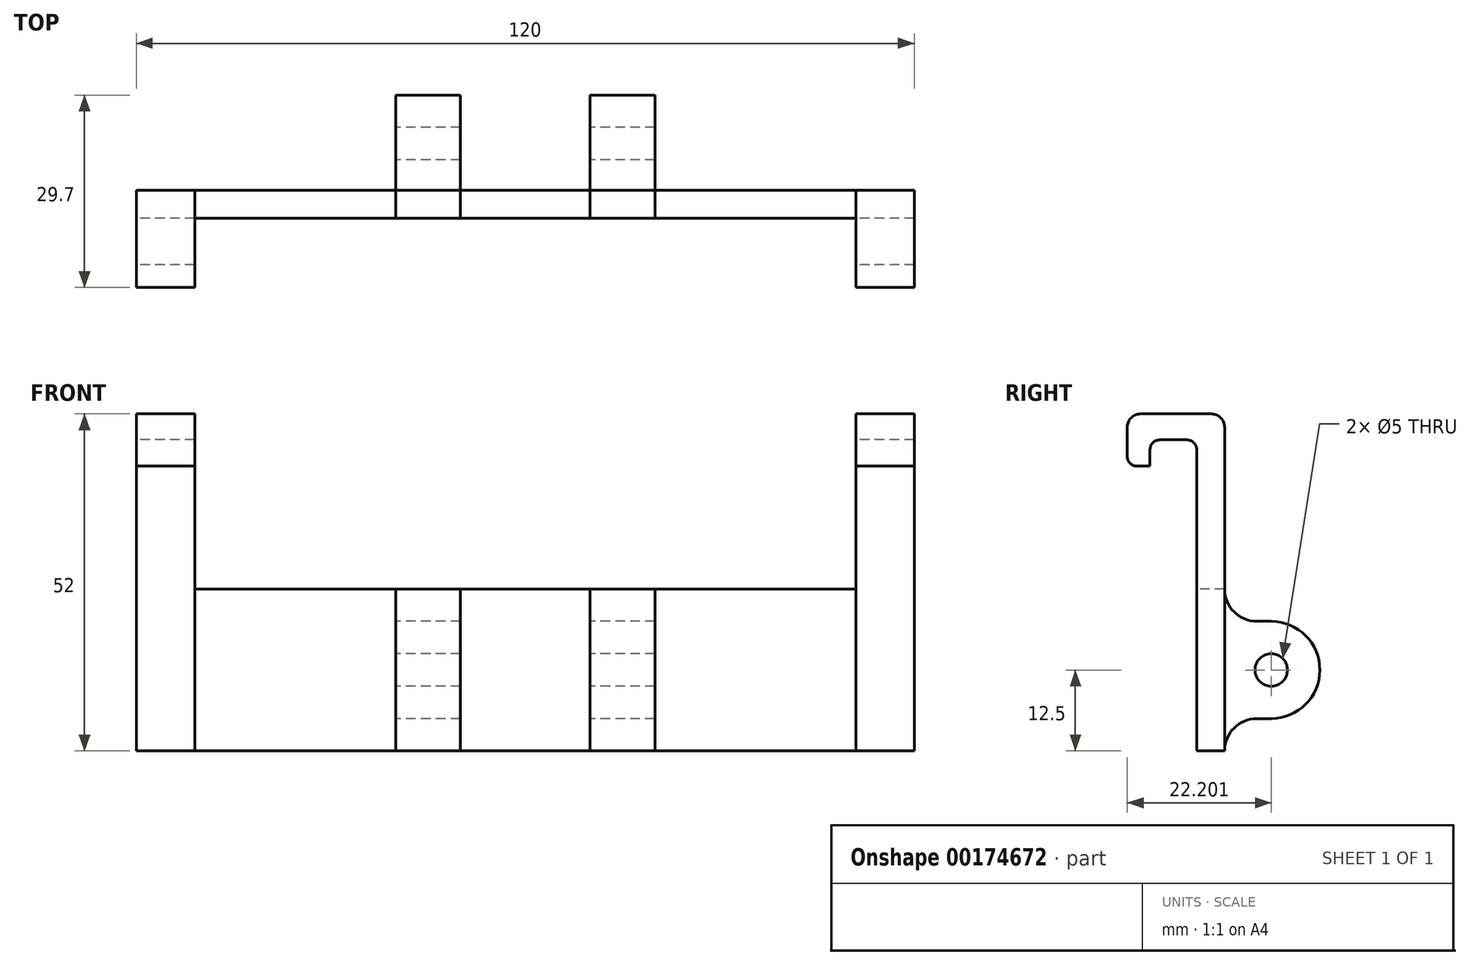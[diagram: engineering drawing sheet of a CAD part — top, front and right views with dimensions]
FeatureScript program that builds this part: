
annotation { "Feature Type Name" : "Feature", "Feature Type Description" : "" }
export const myFeature = defineFeature(function(context is Context, id is Id, definition is map)
    precondition{}
    {
        {
            var Q0;
            Q0=qCreatedBy(makeId("Right.planeOp"),FACE);
            var sketch = newSketch(context, id + "F0", { "sketchPlane" : qUnion([Q0])});
            skLineSegment(sketch, "E0", {"start": v(-3, 12.5) * mm, "end": v(-3, 37.5) * mm});
            skLineSegment(sketch, "E1", {"start": v(-5, 39.5) * mm, "end": v(-16, 39.5) * mm});
            skLineSegment(sketch, "E2", {"start": v(-18, 37.5) * mm, "end": v(-18, 32.94) * mm});
            skLineSegment(sketch, "E3", {"start": v(-16.5, 31.44) * mm, "end": v(-14.5, 31.44) * mm});
            skLineSegment(sketch, "E4", {"start": v(-14.5, 31.44) * mm, "end": v(-14.5, 34) * mm});
            skLineSegment(sketch, "E5", {"start": v(-13, 35.5) * mm, "end": v(-8.8, 35.5) * mm});
            skLineSegment(sketch, "E6", {"start": v(-7.3, 34) * mm, "end": v(-7.3, 0) * mm});
            skArc(sketch, "E7", {"start": v(4.2, -7.5) * mm, "mid": v(11.7, 0) * mm, "end": v(4.2, 7.5) * mm});
            skCircle(sketch, "E8", {"center": v(4.2, 0) * mm, "radius": 2.5 * mm});
            skLineSegment(sketch, "E9", {"start": v(4.2, 7.5) * mm, "end": v(2, 7.5) * mm});
            skPoint(sketch, "E10.newPointA", {"position": v(-3, 2.1) * mm});
            skArc(sketch, "E10.filletArc", {"start": v(-3, 12.5) * mm, "mid": v(-1.54, 8.96) * mm, "end": v(2, 7.5) * mm});
            skPoint(sketch, "E11.visualSharp", {"position": v(-3, 39.5) * mm});
            skArc(sketch, "E11.filletArc", {"start": v(-3, 37.5) * mm, "mid": v(-3.59, 38.91) * mm, "end": v(-5, 39.5) * mm});
            skPoint(sketch, "E12.visualSharp", {"position": v(-18, 39.5) * mm});
            skArc(sketch, "E12.filletArc", {"start": v(-16, 39.5) * mm, "mid": v(-17.41, 38.91) * mm, "end": v(-18, 37.5) * mm});
            skPoint(sketch, "E13.visualSharp", {"position": v(-7.3, 35.5) * mm});
            skArc(sketch, "E13.filletArc", {"start": v(-7.3, 34) * mm, "mid": v(-7.74, 35.06) * mm, "end": v(-8.8, 35.5) * mm});
            skPoint(sketch, "E14.visualSharp", {"position": v(-14.5, 35.5) * mm});
            skArc(sketch, "E14.filletArc", {"start": v(-13, 35.5) * mm, "mid": v(-14.06, 35.06) * mm, "end": v(-14.5, 34) * mm});
            skPoint(sketch, "E15.visualSharp", {"position": v(-18, 31.44) * mm});
            skArc(sketch, "E15.filletArc", {"start": v(-18, 32.94) * mm, "mid": v(-17.56, 31.88) * mm, "end": v(-16.5, 31.44) * mm});
            skLineSegment(sketch, "E16.MirrorCS", {"start": v(-7.3, -34) * mm, "end": v(-7.3, 0) * mm});
            skArc(sketch, "E17.MirrorCS", {"start": v(-7.3, -34) * mm, "mid": v(-7.74, -35.06) * mm, "end": v(-8.8, -35.5) * mm});
            skLineSegment(sketch, "E18.MirrorCS", {"start": v(-13, -35.5) * mm, "end": v(-8.8, -35.5) * mm});
            skArc(sketch, "E19.MirrorCS", {"start": v(-13, -35.5) * mm, "mid": v(-14.06, -35.06) * mm, "end": v(-14.5, -34) * mm});
            skLineSegment(sketch, "E20.MirrorCS", {"start": v(-14.5, -31.44) * mm, "end": v(-14.5, -34) * mm});
            skLineSegment(sketch, "E21.MirrorCS", {"start": v(-16.5, -31.44) * mm, "end": v(-14.5, -31.44) * mm});
            skArc(sketch, "E22.MirrorCS", {"start": v(-18, -32.94) * mm, "mid": v(-17.56, -31.88) * mm, "end": v(-16.5, -31.44) * mm});
            skLineSegment(sketch, "E23.MirrorCS", {"start": v(-18, -37.5) * mm, "end": v(-18, -32.94) * mm});
            skArc(sketch, "E24.MirrorCS", {"start": v(-16, -39.5) * mm, "mid": v(-17.41, -38.91) * mm, "end": v(-18, -37.5) * mm});
            skLineSegment(sketch, "E25.MirrorCS", {"start": v(-5, -39.5) * mm, "end": v(-16, -39.5) * mm});
            skArc(sketch, "E26.MirrorCS", {"start": v(-3, -37.5) * mm, "mid": v(-3.59, -38.91) * mm, "end": v(-5, -39.5) * mm});
            skLineSegment(sketch, "E27.MirrorCS", {"start": v(-3, -12.5) * mm, "end": v(-3, -37.5) * mm});
            skArc(sketch, "E28.MirrorCS", {"start": v(-3, -12.5) * mm, "mid": v(-1.54, -8.96) * mm, "end": v(2, -7.5) * mm});
            skLineSegment(sketch, "E29.MirrorCS", {"start": v(4.2, -7.5) * mm, "end": v(2, -7.5) * mm});
            skLineSegment(sketch, "E30", {"start": v(-3, 12.5) * mm, "end": v(-7.3, 12.5) * mm});
            skPoint(sketch, "E30.endSnap0", {"position": v(-7.3, 17) * mm});
            skLineSegment(sketch, "E31", {"start": v(-3, -12.5) * mm, "end": v(-7.3, -12.5) * mm});
            skLineSegment(sketch, "E32", {"start": v(-3, 12.5) * mm, "end": v(-3, -12.5) * mm});
            skSolve(sketch);
        }
        {
            var Q0;
            Q0=makeQuery(id+"F0.imprint","IMPRINT",FACE,{"disambiguationData":[TD([[makeQuery(id+"F0.imprint","IMPRINT",EDGE,{"derivedFrom":sQuery(id+"F0.wireOp",EDGE,"E0")}),1.0]])]});
            var Q1;
            {var subQ1=sQuery(id+"F0.wireOp",EDGE,"E30");Q1=makeQuery(id+"F0.imprint","IMPRINT",FACE,{"disambiguationData":[TD([[makeQuery(id+"F0.imprint","IMPRINT",EDGE,{"derivedFrom":subQ1}),1.0]])]});}
            var Q2;
            {var subQ1=sQuery(id+"F0.wireOp",EDGE,"E17.MirrorCS");Q2=makeQuery(id+"F0.imprint","IMPRINT",FACE,{"disambiguationData":[TD([[makeQuery(id+"F0.imprint","IMPRINT",EDGE,{"derivedFrom":subQ1}),1.0]])]});}
            extrude(context, id + "F1", {"entities" : qUnion([Q0, Q1, Q2]), "depth" : 9 * mm});
        }
        {
            var Q0;
            Q0=makeQuery(id+"F0.imprint","IMPRINT",FACE,{"disambiguationData":[TD([[makeQuery(id+"F0.imprint","IMPRINT",EDGE,{"derivedFrom":sQuery(id+"F0.wireOp",EDGE,"E7")}),1.0]])]});
            var Q1;
            {var subQ1=sQuery(id+"F0.wireOp",EDGE,"E30");Q1=makeQuery(id+"F0.imprint","IMPRINT",FACE,{"disambiguationData":[TD([[makeQuery(id+"F0.imprint","IMPRINT",EDGE,{"derivedFrom":subQ1}),1.0]])]});}
            extrude(context, id + "F2", {"entities" : qUnion([Q0, Q1]), "depth" : 10 * mm});
        }
        {
            var Q0;
            {var subQ1=sQuery(id+"F0.wireOp",EDGE,"E30");Q0=makeQuery(id+"F0.imprint","IMPRINT",FACE,{"disambiguationData":[TD([[makeQuery(id+"F0.imprint","IMPRINT",EDGE,{"derivedFrom":subQ1}),1.0]])]});}
            extrude(context, id + "F3", {"entities" : qUnion([Q0]), "depth" : 102 * mm});
        }
        {
            var Q0;
            Q0=makeQuery(id+"F1.opExtrude","SWEPT_BODY",BODY,{"disambiguationData":[OSD([sQuery(id+"F0.wireOp",EDGE,"E0"),sQuery(id+"F0.wireOp",EDGE,"E1"),sQuery(id+"F0.wireOp",EDGE,"E2"),sQuery(id+"F0.wireOp",EDGE,"E3"),sQuery(id+"F0.wireOp",EDGE,"E4"),sQuery(id+"F0.wireOp",EDGE,"E5"),sQuery(id+"F0.wireOp",EDGE,"E6"),sQuery(id+"F0.wireOp",EDGE,"E11.filletArc"),sQuery(id+"F0.wireOp",EDGE,"E12.filletArc"),sQuery(id+"F0.wireOp",EDGE,"E13.filletArc"),sQuery(id+"F0.wireOp",EDGE,"E14.filletArc"),sQuery(id+"F0.wireOp",EDGE,"E15.filletArc"),sQuery(id+"F0.wireOp",EDGE,"E16.MirrorCS"),sQuery(id+"F0.wireOp",EDGE,"E17.MirrorCS"),sQuery(id+"F0.wireOp",EDGE,"E18.MirrorCS"),sQuery(id+"F0.wireOp",EDGE,"E19.MirrorCS"),sQuery(id+"F0.wireOp",EDGE,"E20.MirrorCS"),sQuery(id+"F0.wireOp",EDGE,"E21.MirrorCS"),sQuery(id+"F0.wireOp",EDGE,"E22.MirrorCS"),sQuery(id+"F0.wireOp",EDGE,"E23.MirrorCS"),sQuery(id+"F0.wireOp",EDGE,"E24.MirrorCS"),sQuery(id+"F0.wireOp",EDGE,"E25.MirrorCS"),sQuery(id+"F0.wireOp",EDGE,"E26.MirrorCS"),sQuery(id+"F0.wireOp",EDGE,"E27.MirrorCS"),sQuery(id+"F0.wireOp",EDGE,"E32")])]});
            transform(context, id + "F4", {"entities" : qUnion([Q0]), "transformType" : TransformType.TRANSLATION_3D, "dx" : 111 * mm, "dy" : 0 * mm, "dz" : 0 * mm, "makeCopy" : true});
        }
        {
            var Q0;
            Q0=makeQuery(id+"F3.opExtrude","SWEPT_BODY",BODY,{"disambiguationData":[OSD([sQuery(id+"F0.wireOp",EDGE,"E6"),sQuery(id+"F0.wireOp",EDGE,"E16.MirrorCS"),sQuery(id+"F0.wireOp",EDGE,"E30"),sQuery(id+"F0.wireOp",EDGE,"E31"),sQuery(id+"F0.wireOp",EDGE,"E32")])]});
            var Q1;
            Q1=makeQuery(id+"F3.opExtrude","SWEPT_EDGE",EDGE,{"disambiguationData":[OSD([sQuery(id+"F0.wireOp",EDGE,"E0"),sQuery(id+"F0.wireOp",EDGE,"E10.filletArc"),sQuery(id+"F0.wireOp",EDGE,"E30"),sQuery(id+"F0.wireOp",EDGE,"E32")])]});
            transform(context, id + "F5", {"entities" : qUnion([Q0]), "transformType" : TransformType.TRANSLATION_DISTANCE, "transformDirection" : qUnion([Q1]), "distance" : 9 * mm, "oppositeDirection" : true, "makeCopy" : false});
        }
        {
            var Q0;
            Q0=makeQuery(id+"F2.opExtrude","SWEPT_BODY",BODY,{"disambiguationData":[OSD([sQuery(id+"F0.wireOp",EDGE,"E6"),sQuery(id+"F0.wireOp",EDGE,"E7"),sQuery(id+"F0.wireOp",EDGE,"E8"),sQuery(id+"F0.wireOp",EDGE,"E9"),sQuery(id+"F0.wireOp",EDGE,"E10.filletArc"),sQuery(id+"F0.wireOp",EDGE,"E16.MirrorCS"),sQuery(id+"F0.wireOp",EDGE,"E28.MirrorCS"),sQuery(id+"F0.wireOp",EDGE,"E29.MirrorCS"),sQuery(id+"F0.wireOp",EDGE,"E30"),sQuery(id+"F0.wireOp",EDGE,"E31")])]});
            var Q1;
            Q1=makeQuery(id+"F3.opExtrude","SWEPT_EDGE",EDGE,{"disambiguationData":[OSD([sQuery(id+"F0.wireOp",EDGE,"E0"),sQuery(id+"F0.wireOp",EDGE,"E10.filletArc"),sQuery(id+"F0.wireOp",EDGE,"E30"),sQuery(id+"F0.wireOp",EDGE,"E32")])]});
            var Q2;
            Q2=makeQuery(id+"F3.opExtrude","SWEPT_EDGE",EDGE,{"disambiguationData":[OSD([sQuery(id+"F0.wireOp",EDGE,"E0"),sQuery(id+"F0.wireOp",EDGE,"E10.filletArc"),sQuery(id+"F0.wireOp",EDGE,"E30"),sQuery(id+"F0.wireOp",EDGE,"E32")])]});
            transform(context, id + "F6", {"entities" : qUnion([Q0]), "transformType" : TransformType.TRANSLATION_DISTANCE, "transformDirection" : qUnion([Q2]), "distance" : 70 * mm, "oppositeDirection" : true, "makeCopy" : false});
        }
        {
            var Q0;
            Q0=makeQuery(id+"F2.opExtrude","SWEPT_BODY",BODY,{"disambiguationData":[OSD([sQuery(id+"F0.wireOp",EDGE,"E6"),sQuery(id+"F0.wireOp",EDGE,"E7"),sQuery(id+"F0.wireOp",EDGE,"E8"),sQuery(id+"F0.wireOp",EDGE,"E9"),sQuery(id+"F0.wireOp",EDGE,"E10.filletArc"),sQuery(id+"F0.wireOp",EDGE,"E16.MirrorCS"),sQuery(id+"F0.wireOp",EDGE,"E28.MirrorCS"),sQuery(id+"F0.wireOp",EDGE,"E29.MirrorCS"),sQuery(id+"F0.wireOp",EDGE,"E30"),sQuery(id+"F0.wireOp",EDGE,"E31")])]});
            transform(context, id + "F7", {"entities" : qUnion([Q0]), "transformType" : TransformType.TRANSLATION_3D, "dx" : -30 * mm, "dy" : 0 * mm, "dz" : 0 * mm, "makeCopy" : true});
        }
    });
